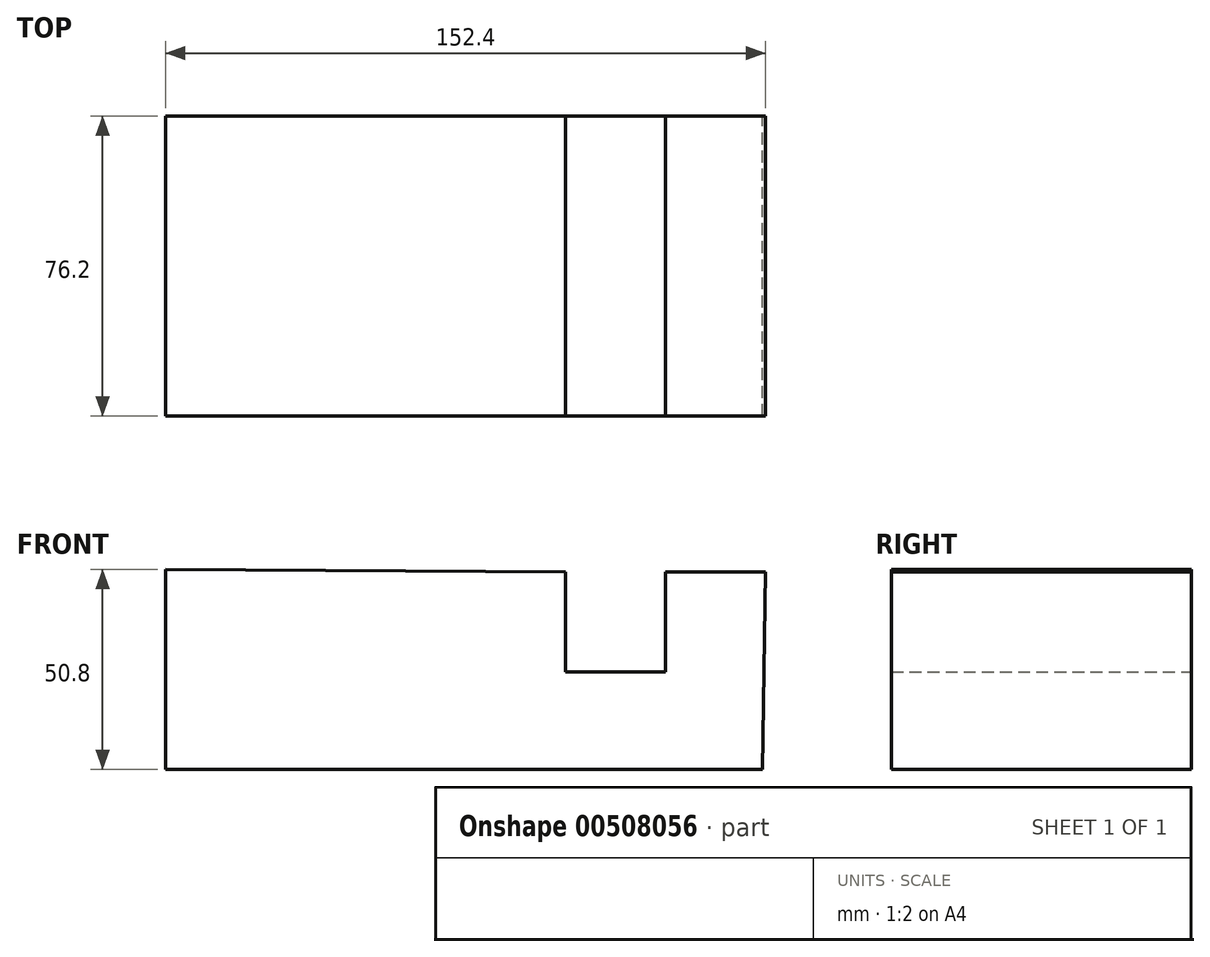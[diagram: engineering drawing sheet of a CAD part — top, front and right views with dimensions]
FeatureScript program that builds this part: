
annotation { "Feature Type Name" : "Feature", "Feature Type Description" : "" }
export const myFeature = defineFeature(function(context is Context, id is Id, definition is map)
    precondition{}
    {
        {
            var Q0;
            Q0=qCreatedBy(makeId("Front.planeOp"),FACE);
            var sketch = newSketch(context, id + "F0", { "sketchPlane" : qUnion([Q0])});
            skLineSegment(sketch, "E0", {"start": v(-74.86, 40.74) * mm, "end": v(26.74, 40.11) * mm});
            skLineSegment(sketch, "E1", {"start": v(26.74, 40.11) * mm, "end": v(26.74, 14.71) * mm});
            skLineSegment(sketch, "E2", {"start": v(26.74, 14.71) * mm, "end": v(52.14, 14.71) * mm});
            skLineSegment(sketch, "E3", {"start": v(52.14, 14.71) * mm, "end": v(52.14, 40.11) * mm});
            skLineSegment(sketch, "E4", {"start": v(52.14, 40.11) * mm, "end": v(77.54, 40.11) * mm});
            skLineSegment(sketch, "E5", {"start": v(77.54, 40.11) * mm, "end": v(76.73, -10.06) * mm});
            skLineSegment(sketch, "E6", {"start": v(-74.86, 40.74) * mm, "end": v(-74.86, -10.06) * mm});
            skLineSegment(sketch, "E7", {"start": v(-74.86, -10.06) * mm, "end": v(76.73, -10.06) * mm});
            skSolve(sketch);
        }
        {
            var Q0;
            Q0=makeQuery(id+"F0.imprint","IMPRINT",FACE,{"disambiguationData":[TD([[makeQuery(id+"F0.imprint","IMPRINT",EDGE,{"derivedFrom":sQuery(id+"F0.wireOp",EDGE,"E0")}),-1.0]])]});
            extrude(context, id + "F1", {"entities" : qUnion([Q0]), "depth" : 76.2 * mm});
        }
    });
